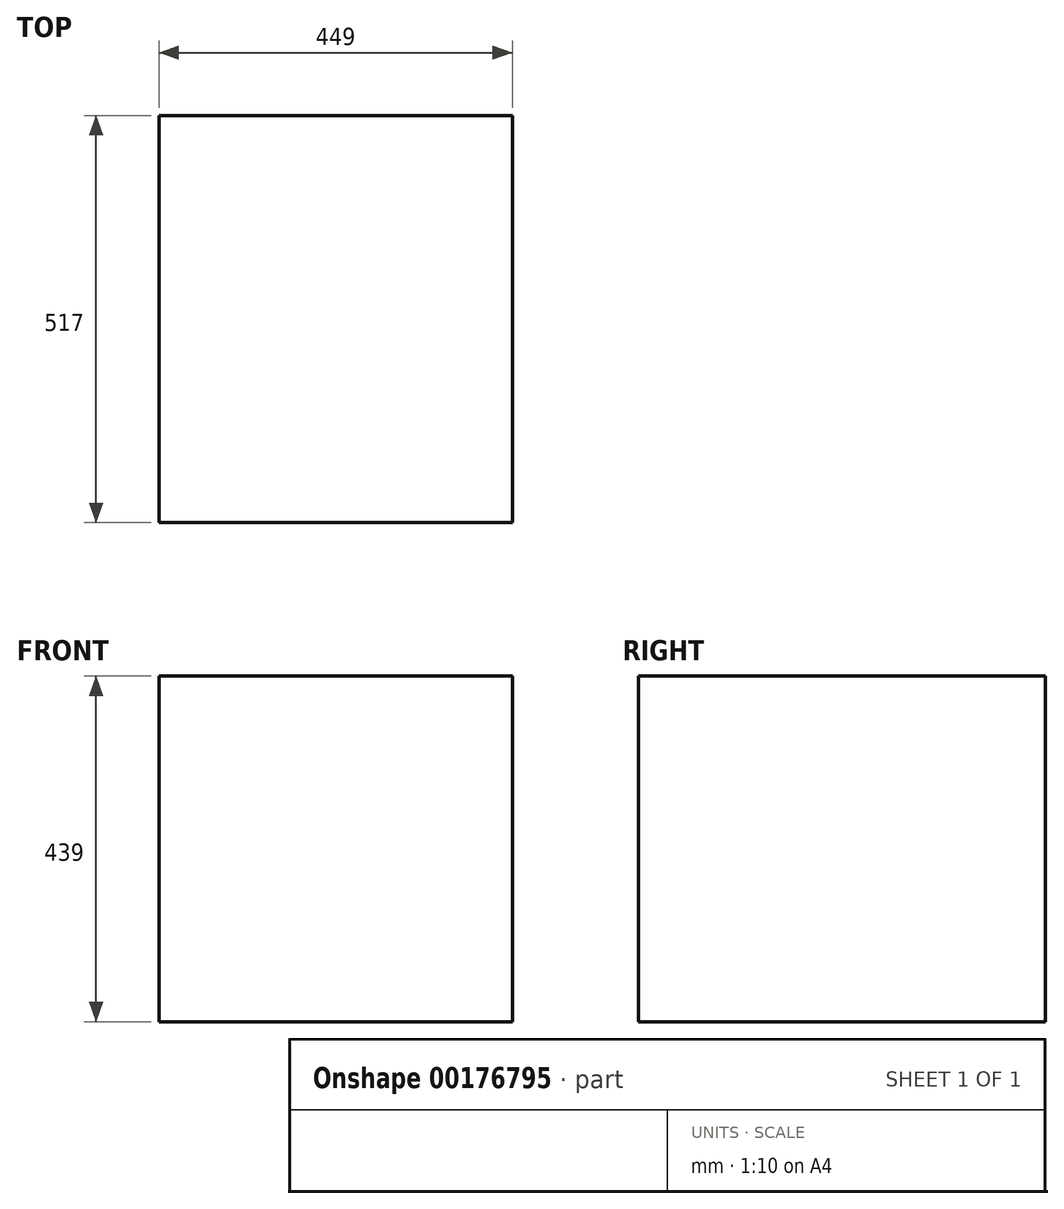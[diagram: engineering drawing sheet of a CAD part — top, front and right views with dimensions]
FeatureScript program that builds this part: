
annotation { "Feature Type Name" : "Feature", "Feature Type Description" : "" }
export const myFeature = defineFeature(function(context is Context, id is Id, definition is map)
    precondition{}
    {
        {
            var Q0;
            Q0=qCreatedBy(makeId("Top.planeOp"),FACE);
            var sketch = newSketch(context, id + "F0", { "sketchPlane" : qUnion([Q0])});
            skLineSegment(sketch, "E0.bottom", {"start": v(-67.92, -59.8) * mm, "end": v(381.08, -59.8) * mm});
            skLineSegment(sketch, "E0.top", {"start": v(-67.92, 457.2) * mm, "end": v(381.08, 457.2) * mm});
            skLineSegment(sketch, "E0.left", {"start": v(-67.92, -59.8) * mm, "end": v(-67.92, 457.2) * mm});
            skLineSegment(sketch, "E0.right", {"start": v(381.08, -59.8) * mm, "end": v(381.08, 457.2) * mm});
            skSolve(sketch);
        }
        {
            var Q0;
            Q0=makeQuery(id+"F0.imprint","IMPRINT",FACE,{"disambiguationData":[TD([[makeQuery(id+"F0.imprint","IMPRINT",EDGE,{"derivedFrom":sQuery(id+"F0.wireOp",EDGE,"E0.bottom")}),1.0]])]});
            extrude(context, id + "F1", {"entities" : qUnion([Q0]), "depth" : 439 * mm});
        }
    });
